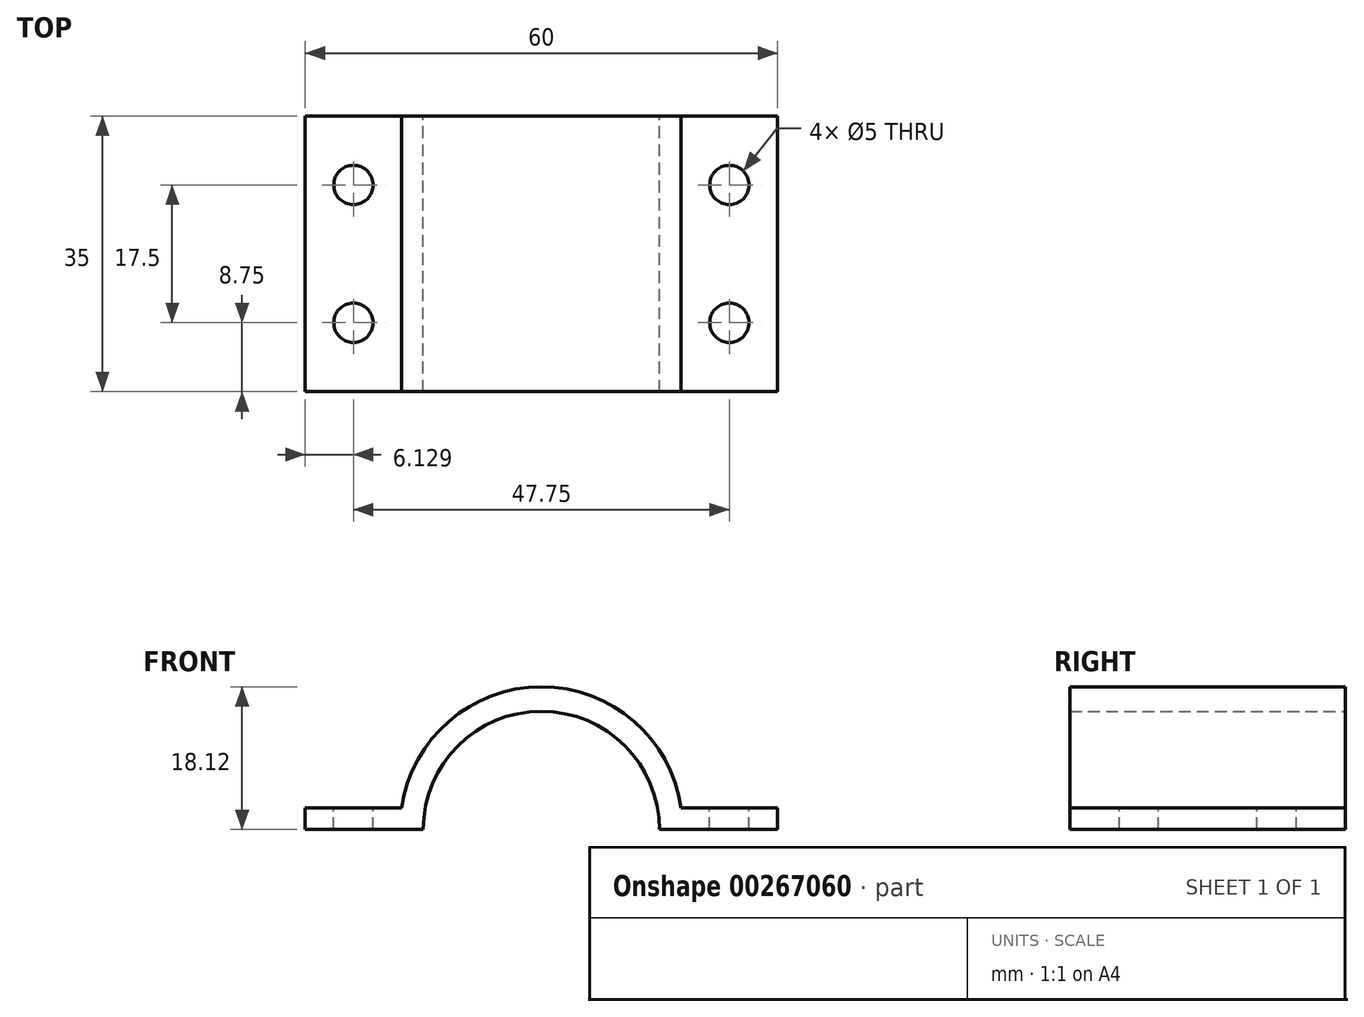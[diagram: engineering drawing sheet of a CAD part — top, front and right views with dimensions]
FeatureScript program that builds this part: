
annotation { "Feature Type Name" : "Feature", "Feature Type Description" : "" }
export const myFeature = defineFeature(function(context is Context, id is Id, definition is map)
    precondition{}
    {
        {
            var Q0;
            Q0=qCreatedBy(makeId("Front.planeOp"),FACE);
            var sketch = newSketch(context, id + "F0", { "sketchPlane" : qUnion([Q0])});
            skLineSegment(sketch, "E0", {"start": v(-19.37, 0) * mm, "end": v(-4.37, 0) * mm});
            skLineSegment(sketch, "E1", {"start": v(-19.37, 0) * mm, "end": v(-19.37, 2.75) * mm});
            skLineSegment(sketch, "E2", {"start": v(-19.37, 2.75) * mm, "end": v(-7.12, 2.75) * mm});
            skLineSegment(sketch, "E3", {"start": v(25.63, 0) * mm, "end": v(40.63, 0) * mm});
            skLineSegment(sketch, "E4", {"start": v(40.63, 0) * mm, "end": v(40.63, 2.75) * mm});
            skLineSegment(sketch, "E5", {"start": v(40.63, 2.75) * mm, "end": v(28.38, 2.75) * mm});
            skArc(sketch, "E6", {"start": v(25.63, 0) * mm, "mid": v(10.63, 15) * mm, "end": v(-4.37, 0) * mm});
            skArc(sketch, "E7", {"start": v(28.38, 2.75) * mm, "mid": v(10.63, 18.12) * mm, "end": v(-7.12, 2.75) * mm});
            skSolve(sketch);
        }
        {
            var Q0;
            Q0 = qSketchRegion(id + "F0", true);
            extrude(context, id + "F1", {"entities" : qUnion([Q0]), "depth" : 35 * mm});
        }
        {
            var Q0;
            Q0=makeQuery(id+"F1.opExtrude","SWEPT_FACE",FACE,{"disambiguationData":[OSD([sQuery(id+"F0.wireOp",EDGE,"E2")])]});
            var sketch = newSketch(context, id + "F2", { "sketchPlane" : qUnion([Q0])});
            skCircle(sketch, "E8", {"center": v(-13.24, -8.75) * mm, "radius": 2.5 * mm});
            skLineSegment(sketch, "E9", {"start": v(-19.37, -17.5) * mm, "end": v(40.63, -17.5) * mm, "construction": true});
            skPoint(sketch, "E10", {"position": v(-13.24, -17.5) * mm});
            skLineSegment(sketch, "E11", {"start": v(-13.24, 0) * mm, "end": v(-13.24, -35) * mm, "construction": true});
            skLineSegment(sketch, "E12.0", {"start": v(40.63, -35) * mm, "end": v(40.63, 0) * mm});
            skPoint(sketch, "E13.orphan", {"position": v(-7.12, -17.5) * mm});
            skPoint(sketch, "E14", {"position": v(10.63, -17.5) * mm});
            skLineSegment(sketch, "E15", {"start": v(10.63, 11.15) * mm, "end": v(10.63, -38) * mm, "construction": true});
            skCircle(sketch, "E16.MirrorC", {"center": v(-13.24, -26.25) * mm, "radius": 2.5 * mm});
            skCircle(sketch, "E17.MirrorC", {"center": v(34.5, -8.75) * mm, "radius": 2.5 * mm});
            skCircle(sketch, "E18.MirrorC", {"center": v(34.5, -26.25) * mm, "radius": 2.5 * mm});
            skSolve(sketch);
        }
        {
            var Q0;
            Q0 = qSketchRegion(id + "F2", true);
            extrude(context, id + "F3", {"entities" : qUnion([Q0]), "operationType" : NewBodyOperationType.REMOVE, "endBound" : BoundingType.THROUGH_ALL, "oppositeDirection" : true, "depth" : 25 * mm});
        }
    });
